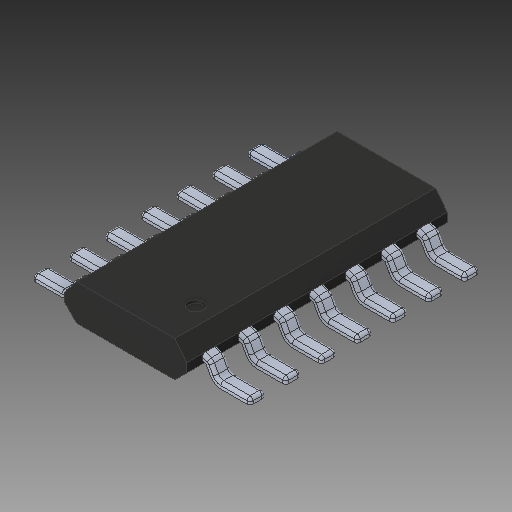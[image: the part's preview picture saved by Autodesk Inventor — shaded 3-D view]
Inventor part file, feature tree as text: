
AUTODESK INVENTOR PART (.ipt)
format: ipt  version: 2018.3 (Build 223284000, 284)  size: 589,824 bytes
history: native  units: mm
features: other x22, mirror x7, fillet x1
ambient origin geometry x8: Origin, YZ Plane, XZ Plane, XY Plane, X Axis, Y Axis, Z Axis, Center Point
bodies: Body1 (feature_tree), Body2 (feature_tree), Body3 (feature_tree), Body4 (feature_tree), Body5 (feature_tree), Body6 (feature_tree), Body7 (feature_tree), Body8 (feature_tree), Body9 (feature_tree), Body10 (feature_tree), Body11 (feature_tree), Body12 (feature_tree), Body13 (feature_tree), Body14 (feature_tree), Body15 (feature_tree)
feature tree (30):
  other  "Sólido1"
  other  "Sólido2"
  other  "Sólido3"
  other  "Sólido4"
  other  "Sólido5"
  other  "Sólido6"
  other  "Sólido7"
  other  "Sólido8"
  other  "Sólido9"
  other  "Sólido10"
  other  "Sólido11"
  other  "Sólido12"
  other  "Sólido13"
  other  "Sólido14"
  other  "Sólido15"
  fillet  "Fillet1"  [1 undecoded]
  other  "LPattern1[1]"
  other  "LPattern1[2]"
  other  "LPattern1[3]"
  mirror  "Mirror1[1]"
  mirror  "Mirror1[2]"
  mirror  "Mirror1[3]"
  mirror  "Mirror1[4]"
  other  "LPattern1[4]"
  other  "LPattern1[5]"
  other  "LPattern1[6]"
  mirror  "Mirror1[5]"
  mirror  "Mirror1[6]"
  mirror  "Mirror1[7]"
  other  "Cut-Extrude1"
note: 1 required parameter value undecoded (feature->parameter linkage not recoverable at this tier; creation-order binding heuristic only, values carry confidence <= 0.55)
